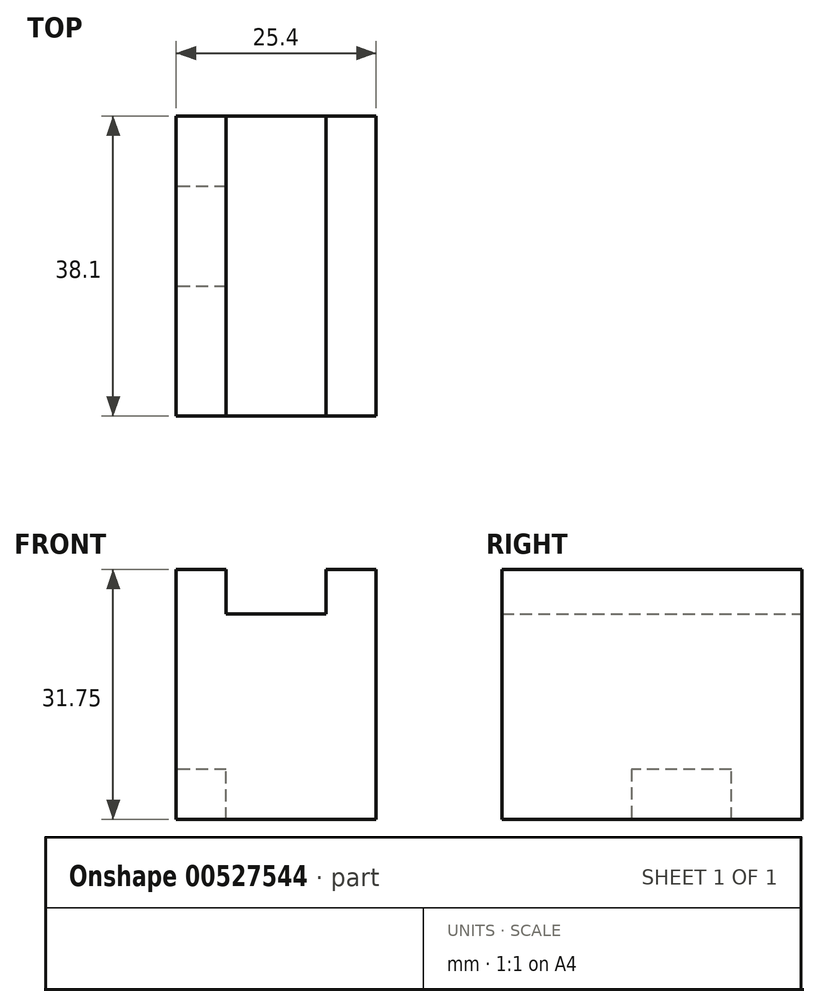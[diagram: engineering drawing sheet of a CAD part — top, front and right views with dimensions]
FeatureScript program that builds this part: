
annotation { "Feature Type Name" : "Feature", "Feature Type Description" : "" }
export const myFeature = defineFeature(function(context is Context, id is Id, definition is map)
    precondition{}
    {
        {
            var Q0;
            Q0=qCreatedBy(makeId("Front.planeOp"),FACE);
            var sketch = newSketch(context, id + "F0", { "sketchPlane" : qUnion([Q0])});
            skLineSegment(sketch, "E0", {"start": v(0, 0) * mm, "end": v(25.4, 0) * mm});
            skLineSegment(sketch, "E1", {"start": v(25.4, 0) * mm, "end": v(25.4, 31.75) * mm});
            skLineSegment(sketch, "E2", {"start": v(25.4, 31.75) * mm, "end": v(19.05, 31.75) * mm});
            skLineSegment(sketch, "E3", {"start": v(19.05, 31.75) * mm, "end": v(19.05, 26.1) * mm});
            skLineSegment(sketch, "E4", {"start": v(19.05, 26.1) * mm, "end": v(6.35, 26.1) * mm});
            skLineSegment(sketch, "E5", {"start": v(6.35, 26.1) * mm, "end": v(6.35, 31.75) * mm});
            skLineSegment(sketch, "E6", {"start": v(6.35, 31.75) * mm, "end": v(0, 31.75) * mm});
            skLineSegment(sketch, "E7", {"start": v(0, 31.75) * mm, "end": v(0, 0) * mm});
            skSolve(sketch);
        }
        {
            var Q0;
            Q0=makeQuery(id+"F0.imprint","IMPRINT",FACE,{"disambiguationData":[TD([[makeQuery(id+"F0.imprint","IMPRINT",EDGE,{"derivedFrom":sQuery(id+"F0.wireOp",EDGE,"E0")}),1.0]])]});
            extrude(context, id + "F1", {"entities" : qUnion([Q0]), "depth" : 38.1 * mm, "offsetDistance" : 25.4 * mm});
        }
        {
            var Q0;
            Q0=makeQuery(id+"F1.opExtrude","SWEPT_FACE",FACE,{"disambiguationData":[OSD([sQuery(id+"F0.wireOp",EDGE,"E7")])]});
            var sketch = newSketch(context, id + "F2", { "sketchPlane" : qUnion([Q0])});
            skLineSegment(sketch, "E8", {"start": v(8.98, 0) * mm, "end": v(8.98, 6.35) * mm});
            skLineSegment(sketch, "E9", {"start": v(8.98, 6.35) * mm, "end": v(21.68, 6.35) * mm});
            skLineSegment(sketch, "E10", {"start": v(21.68, 6.35) * mm, "end": v(21.68, 0) * mm});
            skSolve(sketch);
        }
        {
            var Q0;
            {var subQ0=sQuery(id+"F2.wireOp",EDGE,"E8");Q0=makeQuery(id+"F2.imprint","IMPRINT",FACE,{"disambiguationData":[TD([[makeQuery(id+"F2.imprint","IMPRINT",EDGE,{"derivedFrom":subQ0}),-1.0]])]});}
            extrude(context, id + "F3", {"entities" : qUnion([Q0]), "operationType" : NewBodyOperationType.REMOVE, "oppositeDirection" : true, "depth" : 6.35 * mm, "offsetDistance" : 25.4 * mm});
        }
    });
